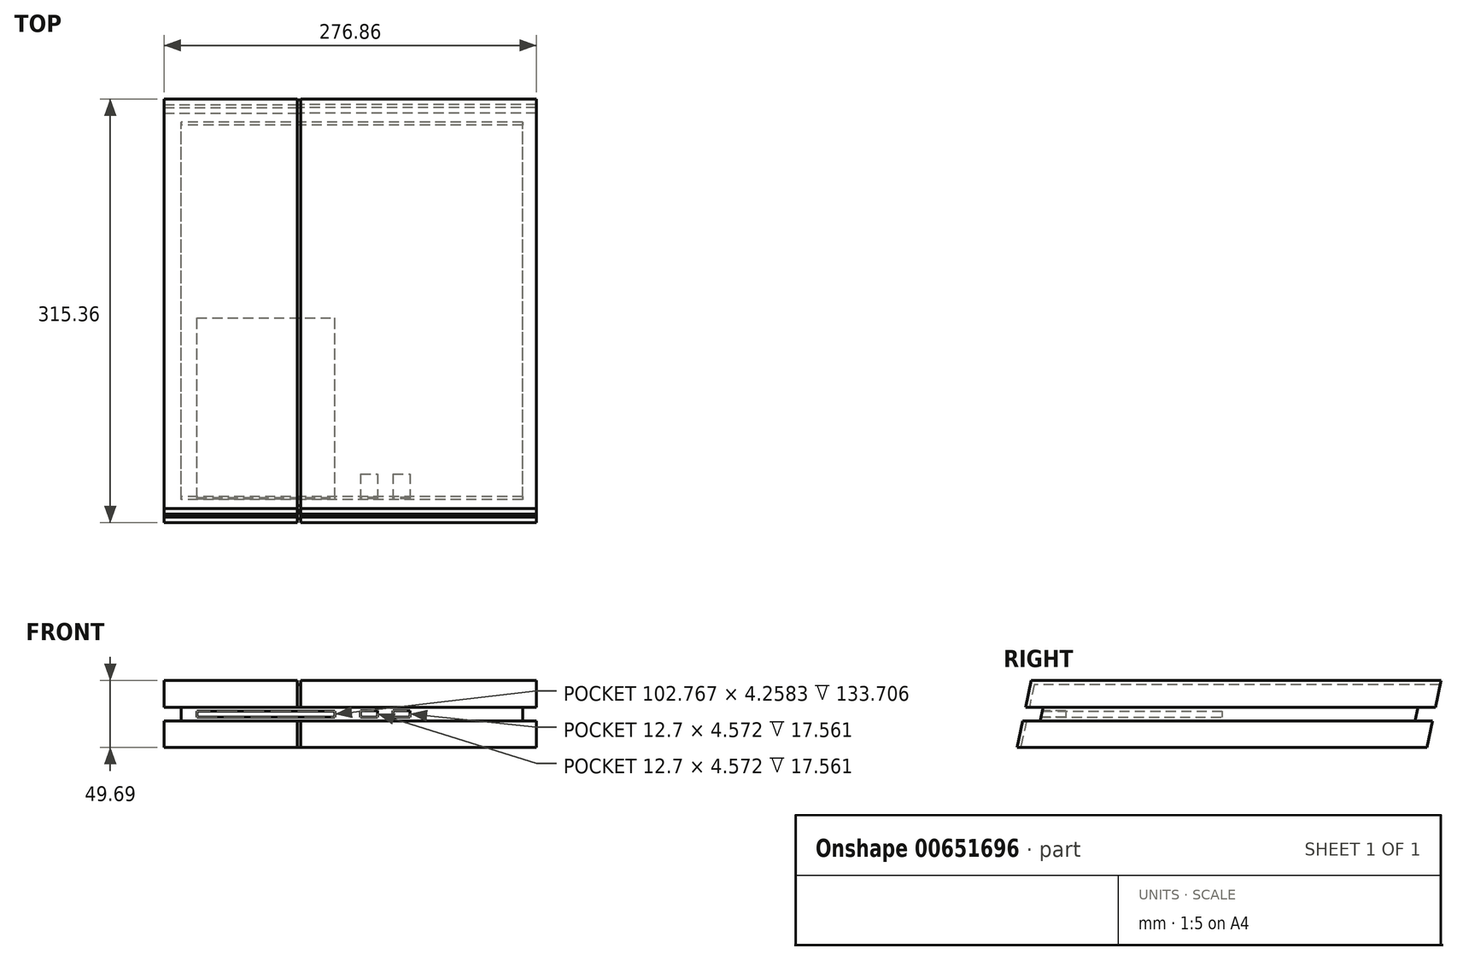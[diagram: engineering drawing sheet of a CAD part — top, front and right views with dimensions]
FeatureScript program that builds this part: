
annotation { "Feature Type Name" : "Feature", "Feature Type Description" : "" }
export const myFeature = defineFeature(function(context is Context, id is Id, definition is map)
    precondition{}
    {
        {
            var Q0;
            Q0=qCreatedBy(makeId("Right.planeOp"),FACE);
            var sketch = newSketch(context, id + "F0", { "sketchPlane" : qUnion([Q0])});
            skLineSegment(sketch, "E0.bottom", {"start": v(-141.84, 49.69) * mm, "end": v(162.96, 49.69) * mm});
            skLineSegment(sketch, "E0.top", {"start": v(-152.4, 0) * mm, "end": v(152.4, 0) * mm});
            skLineSegment(sketch, "E0.left", {"start": v(-141.84, 49.69) * mm, "end": v(-152.4, 0) * mm});
            skLineSegment(sketch, "E0.right", {"start": v(162.96, 49.69) * mm, "end": v(152.4, 0) * mm});
            skLineSegment(sketch, "E1", {"start": v(-147.12, 24.84) * mm, "end": v(157.68, 24.84) * mm});
            skLineSegment(sketch, "E2", {"start": v(-146.04, 29.92) * mm, "end": v(158.76, 29.92) * mm});
            skLineSegment(sketch, "E3", {"start": v(-148.2, 19.76) * mm, "end": v(156.6, 19.76) * mm});
            skLineSegment(sketch, "E4", {"start": v(0, 29.92) * mm, "end": v(0, 24.84) * mm});
            skLineSegment(sketch, "E5", {"start": v(0, 24.84) * mm, "end": v(0, 19.76) * mm});
            skLineSegment(sketch, "E6", {"start": v(-134.14, 24.84) * mm, "end": v(-135.22, 19.76) * mm});
            skLineSegment(sketch, "E7", {"start": v(144.7, 24.84) * mm, "end": v(143.62, 19.76) * mm});
            skLineSegment(sketch, "E8", {"start": v(-134.14, 24.84) * mm, "end": v(-133.06, 29.92) * mm});
            skLineSegment(sketch, "E9", {"start": v(144.7, 24.84) * mm, "end": v(145.78, 29.92) * mm});
            skSolve(sketch);
        }
        {
            var Q0;
            {var subQ5=sQuery(id+"F0.wireOp",EDGE,"E0.bottom");Q0=makeQuery(id+"F0.imprint","IMPRINT",FACE,{"disambiguationData":[TD([[makeQuery(id+"F0.imprint","IMPRINT",EDGE,{"derivedFrom":subQ5}),-1.0]])]});}
            var Q1;
            {var subQ5=sQuery(id+"F0.wireOp",EDGE,"E0.top");Q1=makeQuery(id+"F0.imprint","IMPRINT",FACE,{"disambiguationData":[TD([[makeQuery(id+"F0.imprint","IMPRINT",EDGE,{"derivedFrom":subQ5}),1.0]])]});}
            extrude(context, id + "F1", {"entities" : qUnion([Q0, Q1]), "depth" : 137.16 * mm, "offsetDistance" : 25.4 * mm, "hasSecondDirection" : true, "secondDirectionOppositeDirection" : true, "secondDirectionDepth" : 38.1 * mm});
        }
        {
            var Q0;
            {var subQ0=sQuery(id+"F0.wireOp",EDGE,"E5");Q0=makeQuery(id+"F0.imprint","IMPRINT",FACE,{"disambiguationData":[TD([[makeQuery(id+"F0.imprint","IMPRINT",EDGE,{"derivedFrom":subQ0}),1.0]])]});}
            var Q1;
            {var subQ0=sQuery(id+"F0.wireOp",EDGE,"E4");Q1=makeQuery(id+"F0.imprint","IMPRINT",FACE,{"disambiguationData":[TD([[makeQuery(id+"F0.imprint","IMPRINT",EDGE,{"derivedFrom":subQ0}),1.0]])]});}
            var Q2;
            {var subQ0=sQuery(id+"F0.wireOp",EDGE,"E5");Q2=makeQuery(id+"F0.imprint","IMPRINT",FACE,{"disambiguationData":[TD([[makeQuery(id+"F0.imprint","IMPRINT",EDGE,{"derivedFrom":subQ0}),-1.0]])]});}
            var Q3;
            {var subQ0=sQuery(id+"F0.wireOp",EDGE,"E4");Q3=makeQuery(id+"F0.imprint","IMPRINT",FACE,{"disambiguationData":[TD([[makeQuery(id+"F0.imprint","IMPRINT",EDGE,{"derivedFrom":subQ0}),-1.0]])]});}
            extrude(context, id + "F2", {"entities" : qUnion([Q0, Q1, Q2, Q3]), "depth" : 127 * mm, "offsetDistance" : 25.4 * mm, "hasSecondDirection" : true, "secondDirectionOppositeDirection" : true, "secondDirectionDepth" : 127 * mm});
        }
        {
            var Q0;
            Q0=makeQuery(id+"F1.opExtrude","CAP_FACE",FACE,{"disambiguationData":[OSD([sQuery(id+"F0.wireOp",EDGE,"E0.bottom"),sQuery(id+"F0.wireOp",EDGE,"E0.left"),sQuery(id+"F0.wireOp",EDGE,"E0.right"),sQuery(id+"F0.wireOp",EDGE,"E2")])],"isStart":true});
            var sketch = newSketch(context, id + "F3", { "sketchPlane" : qUnion([Q0])});
            skLineSegment(sketch, "E10", {"start": v(-162.33, 46.7) * mm, "end": v(139.68, 46.7) * mm});
            skLineSegment(sketch, "E11", {"start": v(139.68, 46.7) * mm, "end": v(143.25, 29.92) * mm});
            skLineSegment(sketch, "E12", {"start": v(143.25, 29.92) * mm, "end": v(-158.76, 29.92) * mm});
            skLineSegment(sketch, "E13", {"start": v(-158.76, 29.92) * mm, "end": v(-162.33, 46.7) * mm});
            skLineSegment(sketch, "E14", {"start": v(-156.6, 19.76) * mm, "end": v(145.4, 19.76) * mm});
            skLineSegment(sketch, "E15", {"start": v(145.4, 19.76) * mm, "end": v(149.6, 0) * mm});
            skLineSegment(sketch, "E16", {"start": v(149.6, 0) * mm, "end": v(-152.4, 0) * mm});
            skLineSegment(sketch, "E17", {"start": v(-152.4, 0) * mm, "end": v(-156.6, 19.76) * mm});
            skSolve(sketch);
        }
        {
            var Q0;
            Q0 = qSketchRegion(id + "F3", true);
            extrude(context, id + "F4", {"entities" : qUnion([Q0]), "depth" : 2.54 * mm, "offsetDistance" : 25.4 * mm});
        }
        {
            var Q0;
            Q0=makeQuery(id+"F4.opExtrude","CAP_FACE",FACE,{"disambiguationData":[OSD([sQuery(id+"F3.wireOp",EDGE,"E10"),sQuery(id+"F3.wireOp",EDGE,"E11"),sQuery(id+"F3.wireOp",EDGE,"E12"),sQuery(id+"F3.wireOp",EDGE,"E13")])],"isStart":false});
            var sketch = newSketch(context, id + "F5", { "sketchPlane" : qUnion([Q0])});
            skLineSegment(sketch, "E18.MirrorCS", {"start": v(152.4, 0) * mm, "end": v(141.84, 49.69) * mm});
            skLineSegment(sketch, "E19.MirrorCS", {"start": v(-152.4, 0) * mm, "end": v(-162.96, 49.69) * mm});
            skLineSegment(sketch, "E20.MirrorCS", {"start": v(-156.6, 19.76) * mm, "end": v(148.2, 19.76) * mm});
            skLineSegment(sketch, "E21.MirrorCS", {"start": v(-158.76, 29.92) * mm, "end": v(146.04, 29.92) * mm});
            skLineSegment(sketch, "E22.MirrorCS", {"start": v(-152.4, 0) * mm, "end": v(152.4, 0) * mm});
            skLineSegment(sketch, "E23.MirrorCS", {"start": v(-162.96, 49.69) * mm, "end": v(141.84, 49.69) * mm});
            skSolve(sketch);
        }
        {
            var Q0;
            {var subQ0=sQuery(id+"F5.wireOp",EDGE,"E23.MirrorCS");Q0=makeQuery(id+"F5.imprint","IMPRINT",FACE,{"disambiguationData":[TD([[makeQuery(id+"F5.imprint","IMPRINT",EDGE,{"derivedFrom":subQ0}),-1.0]])]});}
            var Q1;
            {var subQ3=makeQuery(id+"F4.opExtrude","CAP_EDGE",EDGE,{"disambiguationData":[OSD([sQuery(id+"F3.wireOp",EDGE,"E10")])],"isStart":false});Q1=makeQuery(id+"F5.imprint","IMPRINT",FACE,{"disambiguationData":[TD([[makeQuery(id+"F5.imprint","IMPRINT",EDGE,{"derivedFrom":subQ3}),-1.0]])]});}
            var Q2;
            {var subQ2=sQuery(id+"F5.wireOp",EDGE,"E20.MirrorCS");Q2=makeQuery(id+"F5.imprint","IMPRINT",FACE,{"disambiguationData":[TD([[makeQuery(id+"F5.imprint","IMPRINT",EDGE,{"derivedFrom":subQ2}),-1.0]])]});}
            extrude(context, id + "F6", {"entities" : qUnion([Q0, Q1, Q2]), "depth" : 99.06 * mm, "offsetDistance" : 25.4 * mm});
        }
        {
            var Q0;
            Q0=qCreatedBy(makeId("Front.planeOp"),FACE);
            var sketch = newSketch(context, id + "F7", { "sketchPlane" : qUnion([Q0])});
            skLineSegment(sketch, "E24.bottom", {"start": v(-115.34, 26.86) * mm, "end": v(-12.57, 26.86) * mm});
            skLineSegment(sketch, "E24.top", {"start": v(-115.34, 22.6) * mm, "end": v(-12.57, 22.6) * mm});
            skLineSegment(sketch, "E24.left", {"start": v(-115.34, 26.86) * mm, "end": v(-115.34, 22.6) * mm});
            skLineSegment(sketch, "E24.right", {"start": v(-12.57, 26.86) * mm, "end": v(-12.57, 22.6) * mm});
            skSolve(sketch);
        }
        {
            var Q0;
            Q0 = qSketchRegion(id + "F7", true);
            extrude(context, id + "F8", {"entities" : qUnion([Q0]), "operationType" : NewBodyOperationType.REMOVE, "depth" : 152.4 * mm, "offsetDistance" : 25.4 * mm});
        }
        {
            var Q0;
            Q0=qCreatedBy(makeId("Front.planeOp"),FACE);
            cPlane(context, id + "F9", {"entities" : qUnion([Q0]), "cplaneType" : CPlaneType.OFFSET, "offset" : 122.43 * mm, "width" : 152.4 * mm, "height" : 152.4 * mm});
        }
        {
            var Q0;
            Q0=qCreatedBy(id+"F9.planeOp",FACE);
            var sketch = newSketch(context, id + "F10", { "sketchPlane" : qUnion([Q0])});
            skLineSegment(sketch, "E25.bottom", {"start": v(6.35, 27.18) * mm, "end": v(19.05, 27.18) * mm});
            skLineSegment(sketch, "E25.top", {"start": v(6.35, 22.6) * mm, "end": v(19.05, 22.6) * mm});
            skLineSegment(sketch, "E25.left", {"start": v(6.35, 27.18) * mm, "end": v(6.35, 22.6) * mm});
            skLineSegment(sketch, "E25.right", {"start": v(19.05, 27.18) * mm, "end": v(19.05, 22.6) * mm});
            skLineSegment(sketch, "E26.bottom", {"start": v(30.58, 27.18) * mm, "end": v(43.28, 27.18) * mm});
            skLineSegment(sketch, "E26.top", {"start": v(30.58, 22.6) * mm, "end": v(43.28, 22.6) * mm});
            skLineSegment(sketch, "E26.left", {"start": v(30.58, 27.18) * mm, "end": v(30.58, 22.6) * mm});
            skLineSegment(sketch, "E26.right", {"start": v(43.28, 27.18) * mm, "end": v(43.28, 22.6) * mm});
            skSolve(sketch);
        }
        {
            var Q0;
            Q0 = qSketchRegion(id + "F10", true);
            extrude(context, id + "F11", {"entities" : qUnion([Q0]), "operationType" : NewBodyOperationType.REMOVE, "oppositeDirection" : true, "depth" : 6.35 * mm, "offsetDistance" : 25.4 * mm, "hasSecondDirection" : true, "secondDirectionOppositeDirection" : false, "secondDirectionDepth" : 12.7 * mm});
        }
    });
